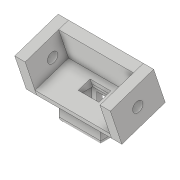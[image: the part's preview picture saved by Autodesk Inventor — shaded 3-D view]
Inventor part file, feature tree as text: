
AUTODESK INVENTOR PART (.ipt)
format: ipt  version: 2018.3 (Build 223284000, 284)  size: 295,936 bytes
history: native  units: in
note: dims shown in document units (in); Inventor stores cm internally (conversion verified against a paired STEP export)
features: extrude x15, sketch x15, plane x1, fillet x1
ambient origin geometry x8: Origin, YZ Plane, XZ Plane, XY Plane, X Axis, Y Axis, Z Axis, Center Point
bodies: Body1 (feature_tree)
feature tree (32):
  extrude  "Extrusion6"  Depth=0.25in TaperAngle=0.0deg
  extrude  "Extrusion8"  Depth=0.5in
  extrude  "Extrusion10"  Depth=0.65in
  extrude  "Extrusion11"  Depth=1.8in TaperAngle=0.0deg
  extrude  "Extrusion12"  Depth=0.25in
  extrude  "Extrusion13"  TaperAngle=0.0deg  [1 undecoded]
  extrude  "Extrusion14"  Depth=1.1in
  extrude  "Extrusion15"  Depth=0.25in TaperAngle=0.0deg
  extrude  "Extrusion16"  Depth=0.125in TaperAngle=0.0deg
  extrude  "Extrusion17"  Depth=1.8in TaperAngle=0.0deg
  plane  "Work Plane1"
  extrude  "Extrusion18"  Depth=0.75in
  extrude  "Extrusion19"  Depth=0.25in TaperAngle=0.0deg
  extrude  "Extrusion20"  Depth=0.125in
  extrude  "Extrusion21"  Depth=0.125in
  extrude  "Extrusion22"  Depth=0.125in
  fillet  "Fillet1"  Radius=0.125in
  sketch  "Sketch8"  dims[d40=1.8in d41=0.0in d50=0.25in d51=0.0in]
  sketch  "Sketch11"  dims[d55=0.3in d56=0.5in]
  sketch  "Sketch13"  dims[d57=0.65in d58=0.65in]
  sketch  "Sketch15"  dims[d59=1.0in d60=0.0in d62=1.8in d63=0.0in]
  sketch  "Sketch17"  dims[d67=0.25in d68=0.1274in]
  sketch  "Sketch19"  dims[d69=0.0in d70=0.0in]
  sketch  "Sketch20"  dims[d73=1.1in d74=0.1274in]
  sketch  "Sketch21"  dims[d76=0.0in d77=0.25in d78=0.0in]
  sketch  "Sketch22"  dims[d79=0.125in d80=0.0in d81=0.125in d82=0.0in]
  sketch  "Sketch23"  dims[d83=1.8in d84=0.0in d85=1.8in d86=0.0in]
  sketch  "Sketch25"  dims[d87=0.75in d88=0.75in]
  sketch  "Sketch26"  dims[d89=0.25in d90=3.0in d91=0.0in]
  sketch  "Sketch27"  dims[d100=-0.1274in d102=0.125in]
  sketch  "Sketch28"  dims[d103=0.125in d104=0.125in]
  sketch  "Sketch29"  dims[d105=0.125in d106=0.125in d107=0.125in d108=0.125in d109=0.125in d110=0.15in d111=0.0in d112=1.0in d113=0.0in d114=1.0in d115=0.0in d116=0.25in d117=0.25in d118=0.325in d119=0.0in d120=0.125in d121=0.125in d122=0.0in d123=0.125in]
note: 1 required parameter value undecoded (feature->parameter linkage not recoverable at this tier; creation-order binding heuristic only, values carry confidence <= 0.55)
